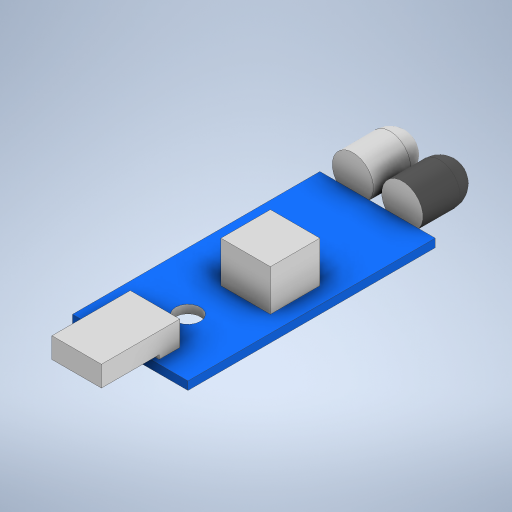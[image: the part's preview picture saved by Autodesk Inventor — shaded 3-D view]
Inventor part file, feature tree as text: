
AUTODESK INVENTOR PART (.ipt)
format: ipt  version: 2024.2 (Build 282272000, 272)  size: 334,336 bytes
history: native  units: mm
features: extrude x6, sketch x6, fillet x1
ambient origin geometry x8: Origin, YZ Plane, XZ Plane, XY Plane, X Axis, Y Axis, Z Axis, Center Point
bodies: Solid1 (feature_tree)
feature tree (13):
  extrude  "Extrusion1"  Depth=30.0mm
  extrude  "Extrusion2"  Depth=5.0mm
  fillet  "Fillet1"  Radius=5.0mm
  extrude  "Extrusion3"  Depth=4.0mm
  extrude  "Extrusion4"  Depth=7.0mm TaperAngle=0.0deg
  extrude  "Extrusion5"  Depth=6.0mm
  extrude  "Extrusion6"  Depth=2.5mm
  sketch  "Sketch1"  dims[d0=14.0mm d1=30.0mm]
  sketch  "Sketch2"  dims[d2=1.0mm d3=0.0mm d4=5.0mm d5=5.0mm]
  sketch  "Sketch3"  dims[d6=2.5mm d7=4.0mm]
  sketch  "Sketch4"  dims[d8=4.0mm d9=7.0mm d10=0.0mm]
  sketch  "Sketch5"  dims[d11=2.5mm d12=6.0mm]
  sketch  "Sketch6"  dims[d13=4.0mm d14=2.5mm d15=0.5mm d16=3.0mm d17=0.0mm d18=2.5mm d19=7.0mm d20=0.0mm d21=6.0mm d22=6.0mm d23=2.0mm d24=12.0mm d25=5.0mm d26=0.0mm d27=3.0mm d28=7.0mm d29=7.0mm d30=0.0mm d31=0.0mm]
